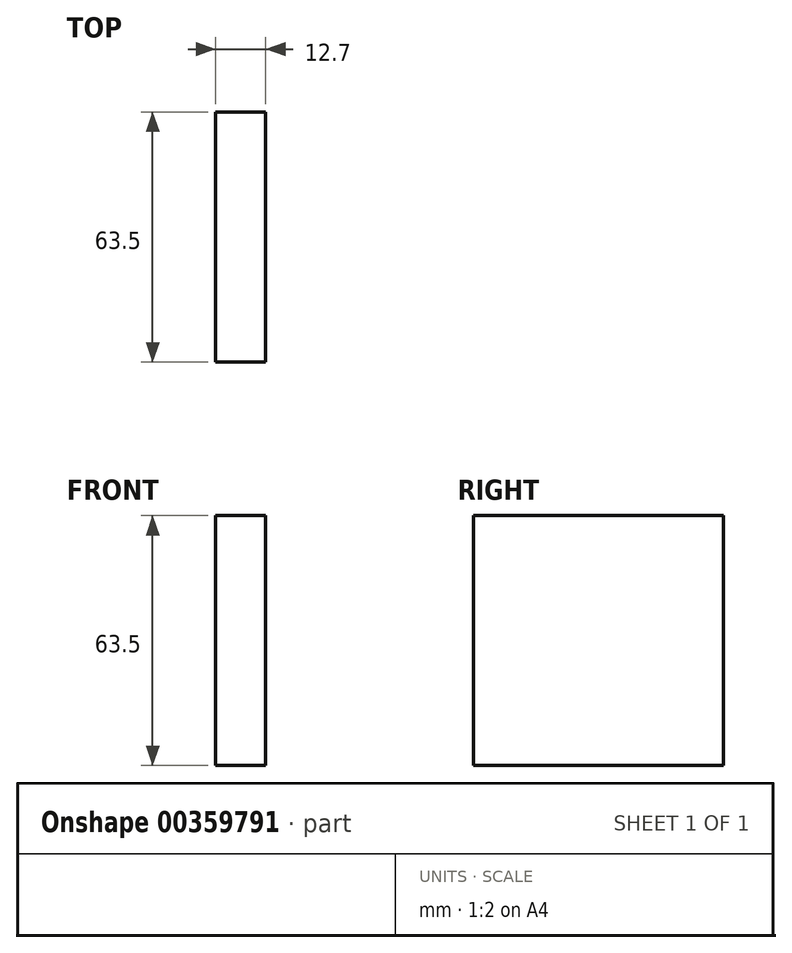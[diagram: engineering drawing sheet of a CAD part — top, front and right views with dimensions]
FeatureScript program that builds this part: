
annotation { "Feature Type Name" : "Feature", "Feature Type Description" : "" }
export const myFeature = defineFeature(function(context is Context, id is Id, definition is map)
    precondition{}
    {
        {
            var Q0;
            Q0=qCreatedBy(makeId("Front.planeOp"),FACE);
            var sketch = newSketch(context, id + "F0", { "sketchPlane" : qUnion([Q0])});
            skLineSegment(sketch, "E0.bottom", {"start": v(12.7, -63.5) * mm, "end": v(0, -63.5) * mm});
            skLineSegment(sketch, "E0.top", {"start": v(12.7, 0) * mm, "end": v(0, 0) * mm});
            skLineSegment(sketch, "E0.left", {"start": v(12.7, -63.5) * mm, "end": v(12.7, 0) * mm});
            skLineSegment(sketch, "E0.right", {"start": v(0, -63.5) * mm, "end": v(0, 0) * mm});
            skSolve(sketch);
        }
        {
            var Q0;
            Q0 = qSketchRegion(id + "F0", true);
            extrude(context, id + "F1", {"entities" : qUnion([Q0]), "depth" : 63.5 * mm});
        }
    });
